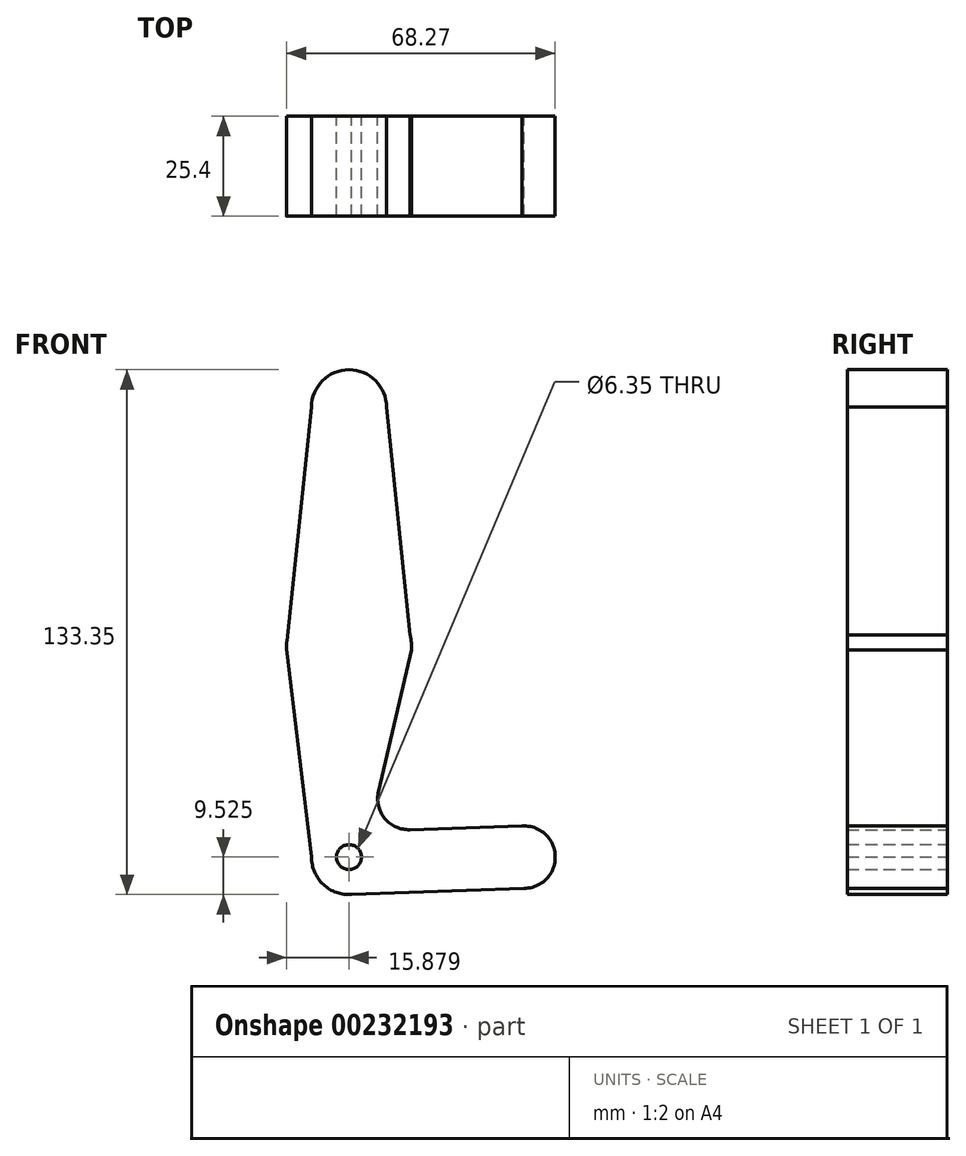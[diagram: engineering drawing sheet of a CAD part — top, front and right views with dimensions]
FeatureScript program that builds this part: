
annotation { "Feature Type Name" : "Feature", "Feature Type Description" : "" }
export const myFeature = defineFeature(function(context is Context, id is Id, definition is map)
    precondition{}
    {
        {
            var Q0;
            Q0=qCreatedBy(makeId("Front.planeOp"),FACE);
            var sketch = newSketch(context, id + "F0", { "sketchPlane" : qUnion([Q0])});
            skLineSegment(sketch, "E0", {"start": v(-29.27, 91.56) * mm, "end": v(-29.27, -22.74) * mm});
            skLineSegment(sketch, "E1", {"start": v(-29.27, -22.74) * mm, "end": v(15.18, -22.74) * mm});
            skCircle(sketch, "E2", {"center": v(-29.27, 91.56) * mm, "radius": 9.53 * mm});
            skCircle(sketch, "E3", {"center": v(-29.27, 30.48) * mm, "radius": 15.88 * mm});
            skCircle(sketch, "E4", {"center": v(-29.27, -22.74) * mm, "radius": 9.53 * mm});
            skCircle(sketch, "E5", {"center": v(15.18, -22.74) * mm, "radius": 7.94 * mm});
            skLineSegment(sketch, "E6", {"start": v(15.18, -22.74) * mm, "end": v(-29.27, -22.74) * mm});
            skLineSegment(sketch, "E7", {"start": v(-38.8, 91.56) * mm, "end": v(-45.23, 30.48) * mm});
            skLineSegment(sketch, "E8", {"start": v(-19.75, 91.56) * mm, "end": v(-13.4, 30.48) * mm});
            skLineSegment(sketch, "E9", {"start": v(-13.4, 29.9) * mm, "end": v(-21.8, -6.02) * mm});
            skLineSegment(sketch, "E10", {"start": v(-45.14, 30.13) * mm, "end": v(-38.8, -22.74) * mm});
            skLineSegment(sketch, "E11", {"start": v(-13.79, -15.77) * mm, "end": v(15.18, -14.8) * mm});
            skLineSegment(sketch, "E12", {"start": v(15.18, -30.67) * mm, "end": v(-29.27, -32.26) * mm});
            skCircle(sketch, "E13", {"center": v(-29.27, 91.56) * mm, "radius": 3.18 * mm});
            skCircle(sketch, "E14", {"center": v(-29.27, 30.48) * mm, "radius": 3.18 * mm});
            skCircle(sketch, "E15", {"center": v(-29.27, -22.74) * mm, "radius": 3.18 * mm});
            skCircle(sketch, "E16", {"center": v(15.18, -22.74) * mm, "radius": 3.18 * mm});
            skCircle(sketch, "E17", {"center": v(-29.27, 68.59) * mm, "radius": 1.59 * mm});
            skPoint(sketch, "E18.newPointA", {"position": v(-29.27, -16.29) * mm});
            skArc(sketch, "E18.filletArc", {"start": v(-21.8, -6.02) * mm, "mid": v(-20.2, -12.87) * mm, "end": v(-13.79, -15.77) * mm});
            skSolve(sketch);
        }
        {
            var Q0;
            {var subQ13=sQuery(id+"F0.wireOp",EDGE,"E18.filletArc");Q0=makeQuery(id+"F0.imprint","IMPRINT",FACE,{"disambiguationData":[TD([[makeQuery(id+"F0.imprint","IMPRINT",EDGE,{"derivedFrom":subQ13}),-1.0]])]});}
            var Q1;
            Q1=makeQuery(id+"F0.imprint","IMPRINT",FACE,{"disambiguationData":[TD([[makeQuery(id+"F0.imprint","IMPRINT",EDGE,{"derivedFrom":sQuery(id+"F0.wireOp",EDGE,"E16")}),-1.0]])]});
            var Q2;
            {var subQ1=sQuery(id+"F0.wireOp",EDGE,"E4");var subQ5=sQuery(id+"F0.wireOp",EDGE,"E0");var subQ6=makeQuery(id+"F0.imprint","INTERSECT",VERTEX,{"derivedFrom":[subQ5,subQ1]});Q2=makeQuery(id+"F0.imprint","IMPRINT",FACE,{"disambiguationData":[TD([[makeQuery(id+"F0.imprint","IMPRINT",EDGE,{"disambiguationData":[TD([[subQ6,-1.0]])],"derivedFrom":subQ5}),-1.0]])]});}
            var Q3;
            {var subQ1=sQuery(id+"F0.wireOp",EDGE,"E3");var subQ4=sQuery(id+"F0.wireOp",EDGE,"E0");var subQ5=makeQuery(id+"F0.imprint","INTERSECT",VERTEX,{"disambiguationData":[OD(0.0)],"derivedFrom":[subQ4,subQ1]});Q3=makeQuery(id+"F0.imprint","IMPRINT",FACE,{"disambiguationData":[TD([[makeQuery(id+"F0.imprint","IMPRINT",EDGE,{"disambiguationData":[TD([[subQ5,-1.0]])],"derivedFrom":subQ4}),-1.0]])]});}
            var Q4;
            {var subQ3=sQuery(id+"F0.wireOp",EDGE,"E0");var subQ5=sQuery(id+"F0.wireOp",EDGE,"E2");var subQ7=makeQuery(id+"F0.imprint","INTERSECT",VERTEX,{"derivedFrom":[subQ3,subQ5]});Q4=makeQuery(id+"F0.imprint","IMPRINT",FACE,{"disambiguationData":[TD([[makeQuery(id+"F0.imprint","IMPRINT",EDGE,{"disambiguationData":[TD([[subQ7,-1.0]])],"derivedFrom":subQ3}),1.0]])]});}
            var Q5;
            {var subQ0=sQuery(id+"F0.wireOp",EDGE,"E3");var subQ1=sQuery(id+"F0.wireOp",EDGE,"E0");var subQ2=makeQuery(id+"F0.imprint","INTERSECT",VERTEX,{"disambiguationData":[OD(1.0)],"derivedFrom":[subQ1,subQ0]});Q5=makeQuery(id+"F0.imprint","IMPRINT",FACE,{"disambiguationData":[TD([[makeQuery(id+"F0.imprint","IMPRINT",EDGE,{"disambiguationData":[TD([[subQ2,-1.0]])],"derivedFrom":subQ1}),-1.0]])]});}
            var Q6;
            {var subQ0=sQuery(id+"F0.wireOp",EDGE,"E4");var subQ1=sQuery(id+"F0.wireOp",EDGE,"E0");var subQ2=makeQuery(id+"F0.imprint","INTERSECT",VERTEX,{"derivedFrom":[subQ1,subQ0]});Q6=makeQuery(id+"F0.imprint","IMPRINT",FACE,{"disambiguationData":[TD([[makeQuery(id+"F0.imprint","IMPRINT",EDGE,{"disambiguationData":[TD([[subQ2,-1.0]])],"derivedFrom":subQ1}),1.0]])]});}
            var Q7;
            {var subQ0=sQuery(id+"F0.wireOp",EDGE,"E12");var subQ1=sQuery(id+"F0.wireOp",EDGE,"E4");var subQ2=makeQuery(id+"F0.imprint","INTERSECT",VERTEX,{"disambiguationData":[OD(1.0)],"derivedFrom":[subQ1,subQ0]});Q7=makeQuery(id+"F0.imprint","IMPRINT",FACE,{"disambiguationData":[TD([[makeQuery(id+"F0.imprint","IMPRINT",EDGE,{"disambiguationData":[TD([[subQ2,-1.0]])],"derivedFrom":subQ1}),-1.0]])]});}
            var Q8;
            Q8=makeQuery(id+"F0.imprint","IMPRINT",FACE,{"disambiguationData":[TD([[makeQuery(id+"F0.imprint","IMPRINT",EDGE,{"derivedFrom":sQuery(id+"F0.wireOp",EDGE,"E16")}),1.0]])]});
            var Q9;
            {var subQ0=sQuery(id+"F0.wireOp",EDGE,"E14");var subQ1=sQuery(id+"F0.wireOp",EDGE,"E0");var subQ2=makeQuery(id+"F0.imprint","INTERSECT",VERTEX,{"disambiguationData":[OD(0.0)],"derivedFrom":[subQ1,subQ0]});Q9=makeQuery(id+"F0.imprint","IMPRINT",FACE,{"disambiguationData":[TD([[makeQuery(id+"F0.imprint","IMPRINT",EDGE,{"disambiguationData":[TD([[subQ2,-1.0]])],"derivedFrom":subQ1}),-1.0]])]});}
            var Q10;
            {var subQ0=sQuery(id+"F0.wireOp",EDGE,"E14");var subQ1=sQuery(id+"F0.wireOp",EDGE,"E0");var subQ2=makeQuery(id+"F0.imprint","INTERSECT",VERTEX,{"disambiguationData":[OD(0.0)],"derivedFrom":[subQ1,subQ0]});Q10=makeQuery(id+"F0.imprint","IMPRINT",FACE,{"disambiguationData":[TD([[makeQuery(id+"F0.imprint","IMPRINT",EDGE,{"disambiguationData":[TD([[subQ2,-1.0]])],"derivedFrom":subQ1}),1.0]])]});}
            var Q11;
            {var subQ0=sQuery(id+"F0.wireOp",EDGE,"E6");var subQ1=sQuery(id+"F0.wireOp",EDGE,"E0");var subQ2=makeQuery(id+"F0.imprint","INTERSECT",VERTEX,{"derivedFrom":[subQ1,subQ0]});Q11=makeQuery(id+"F0.imprint","IMPRINT",FACE,{"disambiguationData":[TD([[makeQuery(id+"F0.imprint","IMPRINT",EDGE,{"disambiguationData":[TD([[subQ2,1.0]])],"derivedFrom":subQ1}),1.0]])]});}
            var Q12;
            {var subQ0=sQuery(id+"F0.wireOp",EDGE,"E6");var subQ1=sQuery(id+"F0.wireOp",EDGE,"E0");var subQ2=makeQuery(id+"F0.imprint","INTERSECT",VERTEX,{"derivedFrom":[subQ1,subQ0]});Q12=makeQuery(id+"F0.imprint","IMPRINT",FACE,{"disambiguationData":[TD([[makeQuery(id+"F0.imprint","IMPRINT",EDGE,{"disambiguationData":[TD([[subQ2,1.0]])],"derivedFrom":subQ1}),-1.0]])]});}
            var Q13;
            {var subQ1=sQuery(id+"F0.wireOp",EDGE,"E3");var subQ3=sQuery(id+"F0.wireOp",EDGE,"E0");var subQ4=makeQuery(id+"F0.imprint","INTERSECT",VERTEX,{"disambiguationData":[OD(0.0)],"derivedFrom":[subQ3,subQ1]});Q13=makeQuery(id+"F0.imprint","IMPRINT",FACE,{"disambiguationData":[TD([[makeQuery(id+"F0.imprint","IMPRINT",EDGE,{"disambiguationData":[TD([[subQ4,-1.0]])],"derivedFrom":subQ3}),1.0]])]});}
            var Q14;
            {var subQ0=sQuery(id+"F0.wireOp",EDGE,"E8");var subQ1=sQuery(id+"F0.wireOp",EDGE,"E3");var subQ2=makeQuery(id+"F0.imprint","INTERSECT",VERTEX,{"disambiguationData":[OD(0.0)],"derivedFrom":[subQ1,subQ0]});Q14=makeQuery(id+"F0.imprint","IMPRINT",FACE,{"disambiguationData":[TD([[makeQuery(id+"F0.imprint","IMPRINT",EDGE,{"disambiguationData":[TD([[subQ2,-1.0]])],"derivedFrom":subQ1}),1.0]])]});}
            var Q15;
            {var subQ0=sQuery(id+"F0.wireOp",EDGE,"E10");var subQ1=sQuery(id+"F0.wireOp",EDGE,"E3");var subQ2=makeQuery(id+"F0.imprint","INTERSECT",VERTEX,{"disambiguationData":[OD(0.0)],"derivedFrom":[subQ1,subQ0]});Q15=makeQuery(id+"F0.imprint","IMPRINT",FACE,{"disambiguationData":[TD([[makeQuery(id+"F0.imprint","IMPRINT",EDGE,{"disambiguationData":[TD([[subQ2,-1.0]])],"derivedFrom":subQ1}),1.0]])]});}
            var Q16;
            {var subQ0=sQuery(id+"F0.wireOp",EDGE,"E9");var subQ1=sQuery(id+"F0.wireOp",EDGE,"E3");var subQ2=makeQuery(id+"F0.imprint","INTERSECT",VERTEX,{"disambiguationData":[OD(0.0)],"derivedFrom":[subQ1,subQ0]});Q16=makeQuery(id+"F0.imprint","IMPRINT",FACE,{"disambiguationData":[TD([[makeQuery(id+"F0.imprint","IMPRINT",EDGE,{"disambiguationData":[TD([[subQ2,1.0]])],"derivedFrom":subQ1}),1.0]])]});}
            var Q17;
            {var subQ0=sQuery(id+"F0.wireOp",EDGE,"E12");var subQ1=sQuery(id+"F0.wireOp",EDGE,"E4");var subQ2=makeQuery(id+"F0.imprint","INTERSECT",VERTEX,{"disambiguationData":[OD(0.0)],"derivedFrom":[subQ1,subQ0]});Q17=makeQuery(id+"F0.imprint","IMPRINT",FACE,{"disambiguationData":[TD([[makeQuery(id+"F0.imprint","IMPRINT",EDGE,{"disambiguationData":[TD([[subQ2,-1.0]])],"derivedFrom":subQ1}),1.0]])]});}
            var Q18;
            {var subQ0=sQuery(id+"F0.wireOp",EDGE,"E11");var subQ1=sQuery(id+"F0.wireOp",EDGE,"E5");var subQ2=makeQuery(id+"F0.imprint","INTERSECT",VERTEX,{"disambiguationData":[OD(0.0)],"derivedFrom":[subQ1,subQ0]});Q18=makeQuery(id+"F0.imprint","IMPRINT",FACE,{"disambiguationData":[TD([[makeQuery(id+"F0.imprint","IMPRINT",EDGE,{"disambiguationData":[TD([[subQ2,-1.0]])],"derivedFrom":subQ1}),1.0]])]});}
            var Q19;
            {var subQ0=sQuery(id+"F0.wireOp",EDGE,"E17");var subQ1=sQuery(id+"F0.wireOp",EDGE,"E0");var subQ2=makeQuery(id+"F0.imprint","INTERSECT",VERTEX,{"disambiguationData":[OD(0.0)],"derivedFrom":[subQ1,subQ0]});Q19=makeQuery(id+"F0.imprint","IMPRINT",FACE,{"disambiguationData":[TD([[makeQuery(id+"F0.imprint","IMPRINT",EDGE,{"disambiguationData":[TD([[subQ2,-1.0]])],"derivedFrom":subQ1}),-1.0]])]});}
            var Q20;
            {var subQ0=sQuery(id+"F0.wireOp",EDGE,"E17");var subQ1=sQuery(id+"F0.wireOp",EDGE,"E0");var subQ2=makeQuery(id+"F0.imprint","INTERSECT",VERTEX,{"disambiguationData":[OD(0.0)],"derivedFrom":[subQ1,subQ0]});Q20=makeQuery(id+"F0.imprint","IMPRINT",FACE,{"disambiguationData":[TD([[makeQuery(id+"F0.imprint","IMPRINT",EDGE,{"disambiguationData":[TD([[subQ2,-1.0]])],"derivedFrom":subQ1}),1.0]])]});}
            var Q21;
            {var subQ3=sQuery(id+"F0.wireOp",EDGE,"E0");var subQ5=sQuery(id+"F0.wireOp",EDGE,"E2");var subQ7=makeQuery(id+"F0.imprint","INTERSECT",VERTEX,{"derivedFrom":[subQ3,subQ5]});Q21=makeQuery(id+"F0.imprint","IMPRINT",FACE,{"disambiguationData":[TD([[makeQuery(id+"F0.imprint","IMPRINT",EDGE,{"disambiguationData":[TD([[subQ7,-1.0]])],"derivedFrom":subQ3}),-1.0]])]});}
            var Q22;
            Q22=makeQuery(id+"F0.imprint","IMPRINT",FACE,{"disambiguationData":[TD([[makeQuery(id+"F0.imprint","IMPRINT",EDGE,{"derivedFrom":sQuery(id+"F0.wireOp",EDGE,"E13")}),-1.0]])]});
            var Q23;
            Q23=makeQuery(id+"F0.imprint","IMPRINT",FACE,{"disambiguationData":[TD([[makeQuery(id+"F0.imprint","IMPRINT",EDGE,{"derivedFrom":sQuery(id+"F0.wireOp",EDGE,"E13")}),1.0]])]});
            extrude(context, id + "F1", {"entities" : qUnion([Q0, Q1, Q2, Q3, Q4, Q5, Q6, Q7, Q8, Q9, Q10, Q11, Q12, Q13, Q14, Q15, Q16, Q17, Q18, Q19, Q20, Q21, Q22, Q23]), "depth" : 25.4 * mm});
        }
    });
